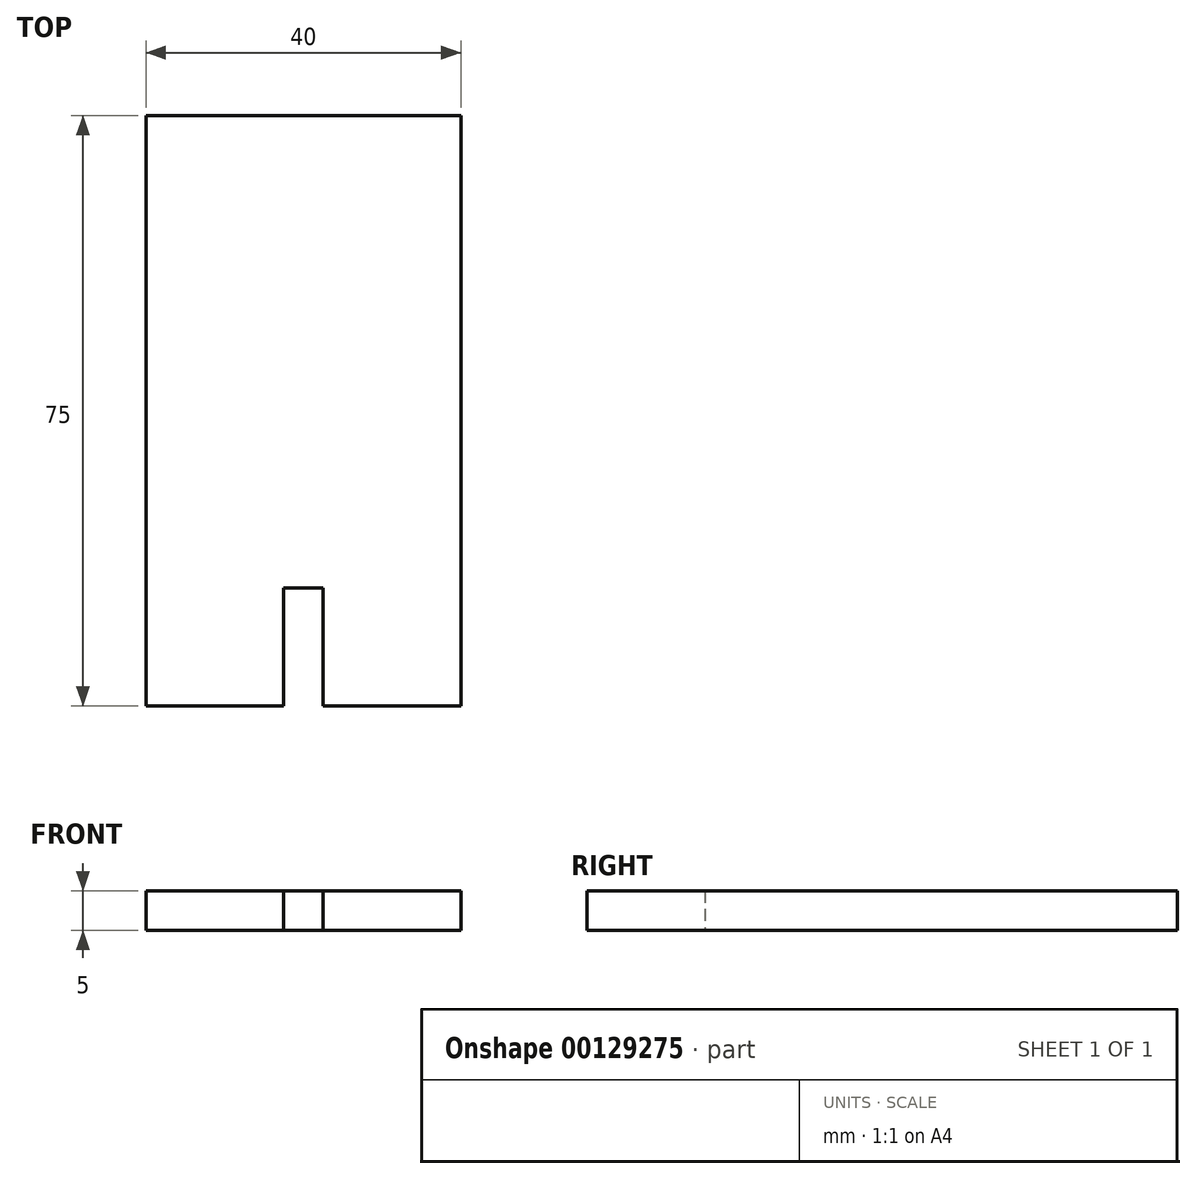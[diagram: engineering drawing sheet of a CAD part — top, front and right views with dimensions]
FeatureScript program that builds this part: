
annotation { "Feature Type Name" : "Feature", "Feature Type Description" : "" }
export const myFeature = defineFeature(function(context is Context, id is Id, definition is map)
    precondition{}
    {
        {
            var Q0;
            Q0=qCreatedBy(makeId("Top.planeOp"),FACE);
            var sketch = newSketch(context, id + "F0", { "sketchPlane" : qUnion([Q0])});
            skLineSegment(sketch, "E0.bottom", {"start": v(0, 0) * mm, "end": v(-40, 0) * mm});
            skLineSegment(sketch, "E0.top", {"start": v(0, 75) * mm, "end": v(-40, 75) * mm});
            skLineSegment(sketch, "E0.left", {"start": v(0, 0) * mm, "end": v(0, 75) * mm});
            skLineSegment(sketch, "E0.right", {"start": v(-40, 0) * mm, "end": v(-40, 75) * mm});
            skLineSegment(sketch, "E1", {"start": v(-22.5, 0) * mm, "end": v(-22.5, 15) * mm});
            skLineSegment(sketch, "E2", {"start": v(-22.5, 15) * mm, "end": v(-17.5, 15) * mm});
            skLineSegment(sketch, "E3", {"start": v(-17.5, 15) * mm, "end": v(-17.5, 0) * mm});
            skSolve(sketch);
        }
        {
            var Q0;
            Q0=makeQuery(id+"F0.imprint","IMPRINT",FACE,{"disambiguationData":[TD([[makeQuery(id+"F0.imprint","IMPRINT",EDGE,{"derivedFrom":sQuery(id+"F0.wireOp",EDGE,"E0.top")}),1.0]])]});
            extrude(context, id + "F1", {"entities" : qUnion([Q0]), "depth" : 5 * mm});
        }
    });
